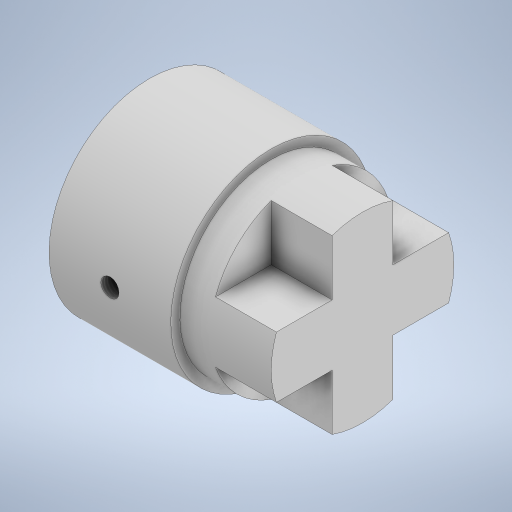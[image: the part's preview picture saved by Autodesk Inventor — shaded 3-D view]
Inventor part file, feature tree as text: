
AUTODESK INVENTOR PART (.ipt)
format: ipt  version: 2023 (Build 270158000, 158)  size: 284,672 bytes
history: native  units: mm
features: sketch x3, extrude x2, other x1, revolve x1, thread x1
ambient origin geometry x8: Origin, YZ Plane, XZ Plane, XY Plane, X Axis, Y Axis, Z Axis, Center Point
bodies: Body1 (feature_tree)
feature tree (8):
  other  "Твердое тело1"
  revolve  "Вращение1"
  extrude  "Выдавливание1"  Depth=20.0mm
  thread  "Резьба1"
  extrude  "Выдавливание2"  Depth=12.5mm
  sketch  "Эскиз1"
  sketch  "Эскиз2"
  sketch  "Эскиз3"
